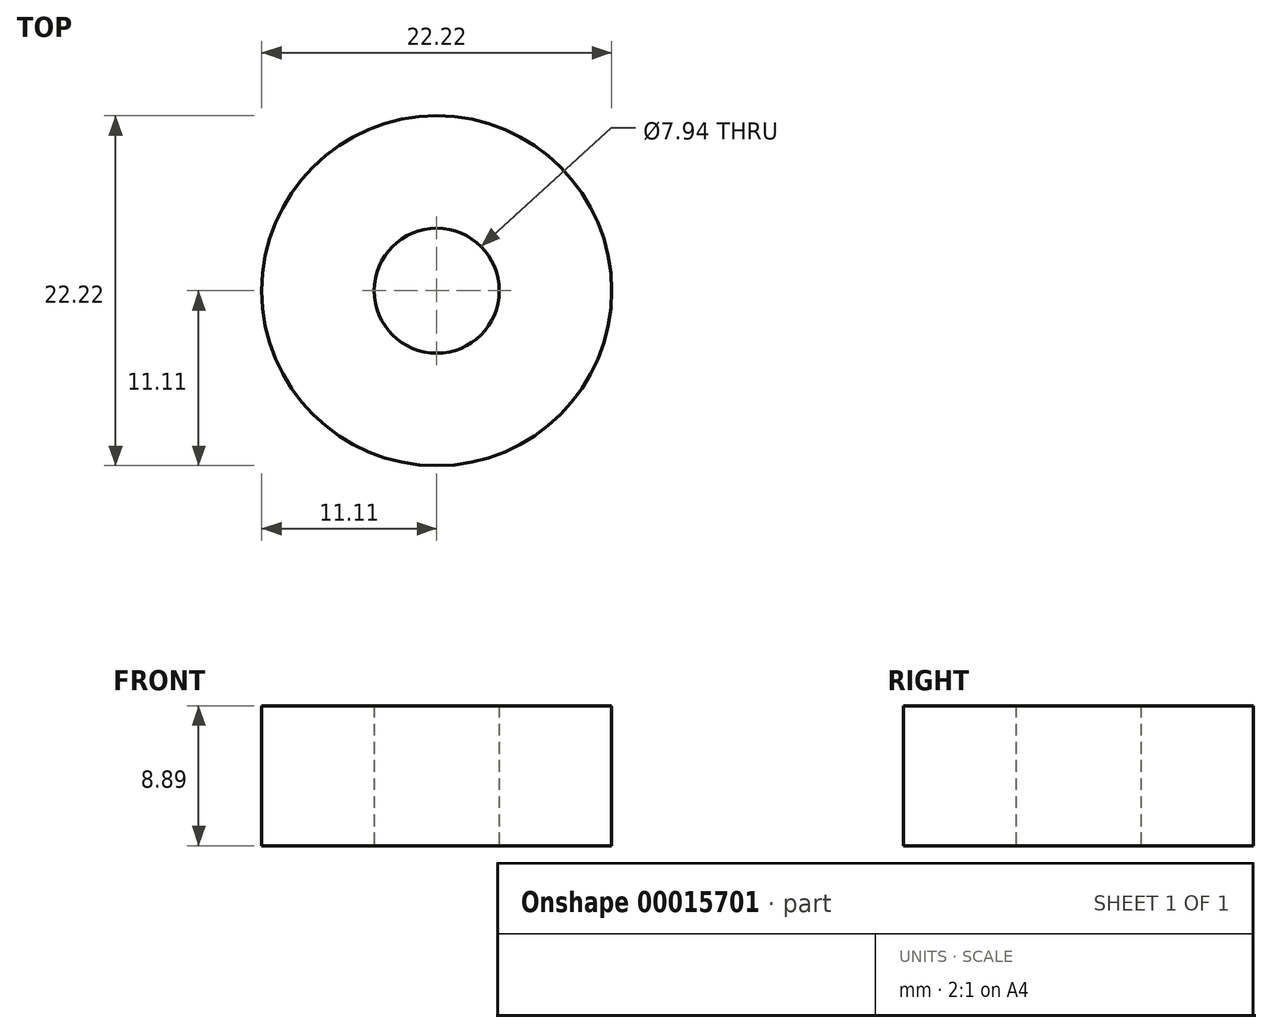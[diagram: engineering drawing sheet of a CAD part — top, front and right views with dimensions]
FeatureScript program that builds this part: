
annotation { "Feature Type Name" : "Feature", "Feature Type Description" : "" }
export const myFeature = defineFeature(function(context is Context, id is Id, definition is map)
    precondition{}
    {
        {
            var Q0;
            Q0=qCreatedBy(makeId("Top.planeOp"),FACE);
            var sketch = newSketch(context, id + "F0", { "sketchPlane" : qUnion([Q0])});
            skCircle(sketch, "E0", {"center": v(0, 0) * mm, "radius": 3.97 * mm});
            skCircle(sketch, "E1", {"center": v(0, 0) * mm, "radius": 11.11 * mm});
            skSolve(sketch);
        }
        {
            var Q0;
            Q0 = qSketchRegion(id + "F0", true);
            extrude(context, id + "F1", {"entities" : qUnion([Q0]), "depth" : 8.9 * mm});
        }
    });
